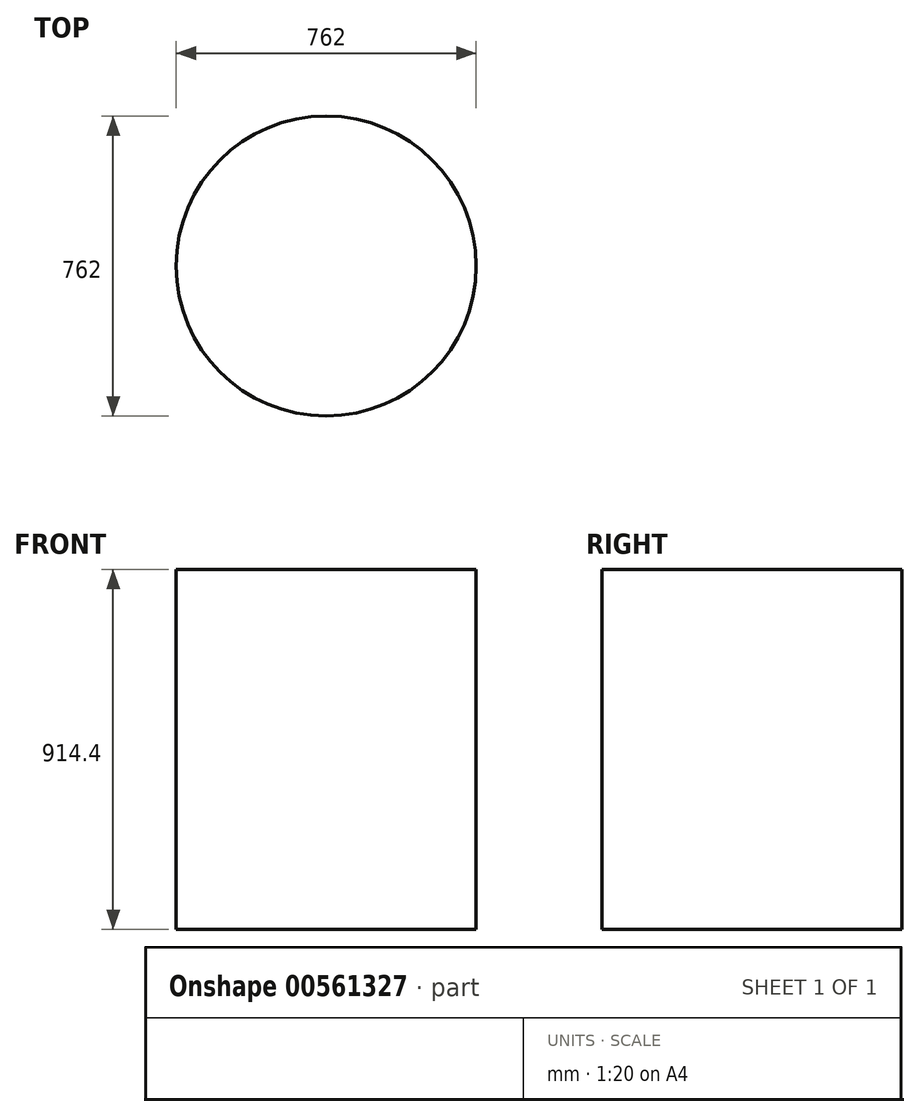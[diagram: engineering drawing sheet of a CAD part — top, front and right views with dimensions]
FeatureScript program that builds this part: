
annotation { "Feature Type Name" : "Feature", "Feature Type Description" : "" }
export const myFeature = defineFeature(function(context is Context, id is Id, definition is map)
    precondition{}
    {
        {
            var Q0;
            Q0=qCreatedBy(makeId("Top.planeOp"),FACE);
            var sketch = newSketch(context, id + "F0", { "sketchPlane" : qUnion([Q0])});
            skCircle(sketch, "E0", {"center": v(-375.96, 25.47) * mm, "radius": 381 * mm});
            skSolve(sketch);
        }
        {
            var Q0;
            Q0 = qSketchRegion(id + "F0", true);
            extrude(context, id + "F1", {"entities" : qUnion([Q0]), "depth" : 914.4 * mm, "offsetDistance" : 30.48 * mm});
        }
    });
